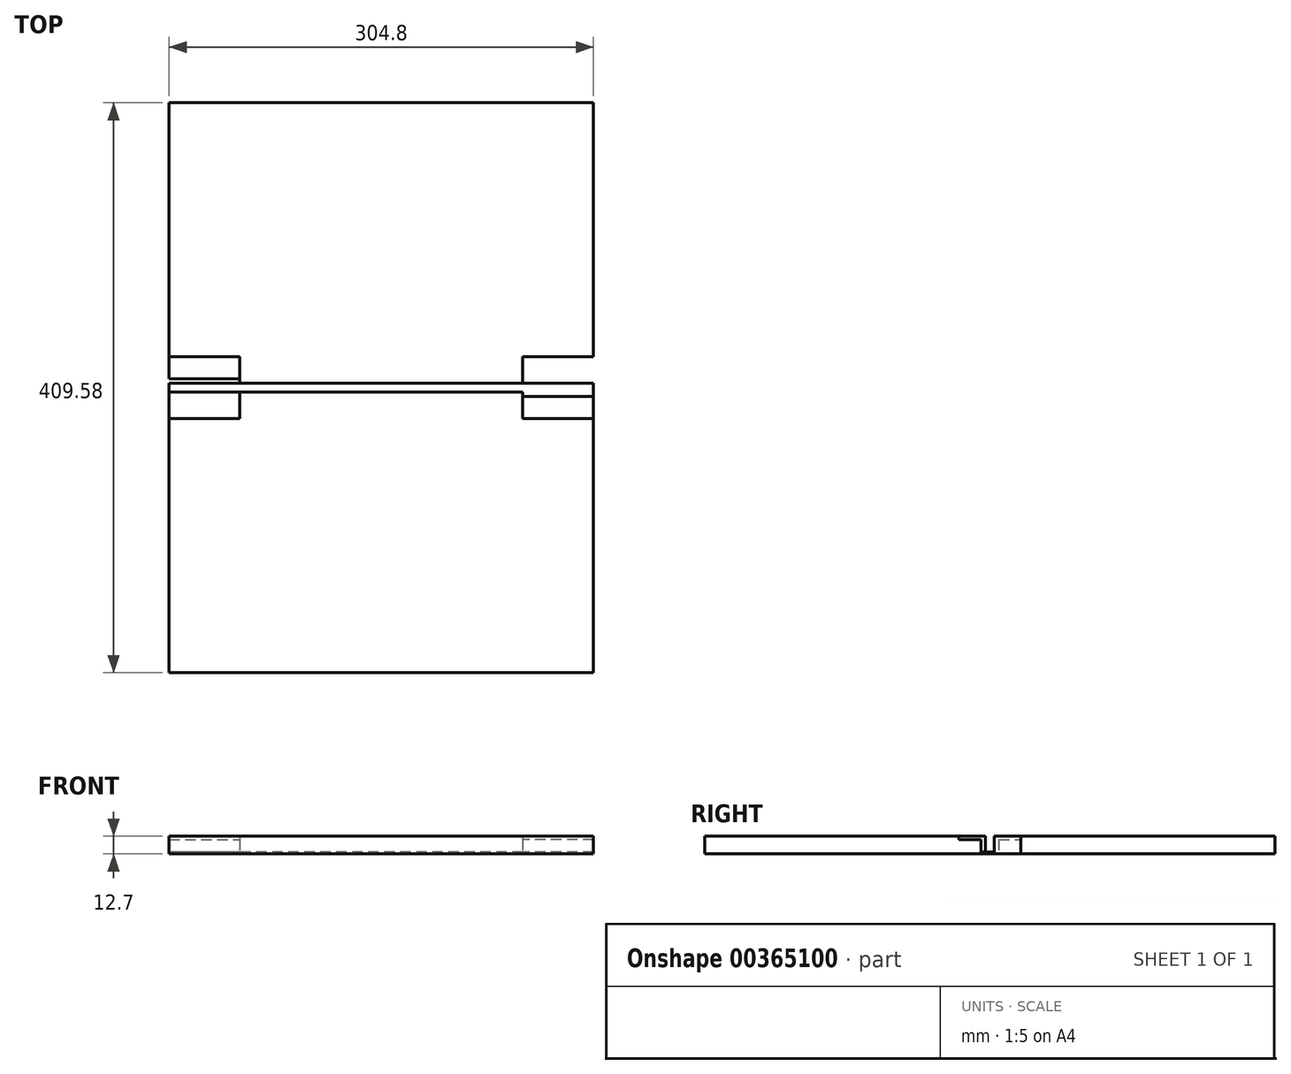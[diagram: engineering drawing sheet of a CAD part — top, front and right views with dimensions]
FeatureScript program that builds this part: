
annotation { "Feature Type Name" : "Feature", "Feature Type Description" : "" }
export const myFeature = defineFeature(function(context is Context, id is Id, definition is map)
    precondition{}
    {
        {
            var Q0;
            Q0=qCreatedBy(makeId("Top.planeOp"),FACE);
            var sketch = newSketch(context, id + "F0", { "sketchPlane" : qUnion([Q0])});
            skLineSegment(sketch, "E0.bottom", {"start": v(152.4, -204.79) * mm, "end": v(-152.4, -204.79) * mm});
            skLineSegment(sketch, "E0.top", {"start": v(152.4, 204.79) * mm, "end": v(-152.4, 204.79) * mm});
            skLineSegment(sketch, "E0.left", {"start": v(152.4, -204.79) * mm, "end": v(152.4, 204.79) * mm});
            skLineSegment(sketch, "E0.right", {"start": v(-152.4, -204.79) * mm, "end": v(-152.4, 204.79) * mm});
            skPoint(sketch, "E0.middle", {"position": v(0, 0) * mm});
            skLineSegment(sketch, "E1.bottom", {"start": v(152.4, -3.18) * mm, "end": v(-152.4, -3.18) * mm});
            skLineSegment(sketch, "E1.top", {"start": v(152.4, 3.18) * mm, "end": v(-152.4, 3.18) * mm});
            skLineSegment(sketch, "E1.left", {"start": v(152.4, -3.18) * mm, "end": v(152.4, 3.18) * mm});
            skLineSegment(sketch, "E1.right", {"start": v(-152.4, -3.18) * mm, "end": v(-152.4, 3.18) * mm});
            skPoint(sketch, "E2", {"position": v(-152.4, 0) * mm});
            skLineSegment(sketch, "E3", {"start": v(-152.4, 0) * mm, "end": v(0, 0) * mm});
            skLineSegment(sketch, "E4.bottom", {"start": v(-152.4, 3.18) * mm, "end": v(-101.6, 3.18) * mm});
            skLineSegment(sketch, "E4.top", {"start": v(-152.4, 22.23) * mm, "end": v(-101.6, 22.23) * mm});
            skLineSegment(sketch, "E4.left", {"start": v(-152.4, 3.18) * mm, "end": v(-152.4, 22.23) * mm});
            skLineSegment(sketch, "E4.right", {"start": v(-101.6, 3.18) * mm, "end": v(-101.6, 22.22) * mm});
            skLineSegment(sketch, "E5.top", {"start": v(-152.4, 6.35) * mm, "end": v(-101.6, 6.35) * mm});
            skLineSegment(sketch, "E5.left", {"start": v(-152.4, 3.18) * mm, "end": v(-152.4, 6.35) * mm});
            skLineSegment(sketch, "E5.right", {"start": v(-101.6, 3.18) * mm, "end": v(-101.6, 6.35) * mm});
            skLineSegment(sketch, "E6.MirrorCS", {"start": v(-152.4, 3.18) * mm, "end": v(-152.4, -3.18) * mm});
            skLineSegment(sketch, "E7.MirrorCS", {"start": v(-101.6, -3.18) * mm, "end": v(-101.6, -22.22) * mm});
            skLineSegment(sketch, "E8.MirrorCS", {"start": v(-101.6, -3.18) * mm, "end": v(-101.6, -6.35) * mm});
            skLineSegment(sketch, "E9.MirrorCS", {"start": v(-152.4, -3.18) * mm, "end": v(-152.4, -22.23) * mm});
            skLineSegment(sketch, "E10.MirrorCS", {"start": v(-152.4, -3.18) * mm, "end": v(-152.4, -6.35) * mm});
            skLineSegment(sketch, "E11.MirrorCS", {"start": v(-152.4, -6.35) * mm, "end": v(-101.6, -6.35) * mm});
            skLineSegment(sketch, "E12.MirrorCS", {"start": v(-152.4, -22.23) * mm, "end": v(-101.6, -22.22) * mm});
            skLineSegment(sketch, "E13.MirrorCS", {"start": v(-152.4, -3.18) * mm, "end": v(-101.6, -3.17) * mm});
            skPoint(sketch, "E14", {"position": v(0, 3.18) * mm});
            skPoint(sketch, "E15.MirrorP", {"position": v(152.4, 0) * mm});
            skLineSegment(sketch, "E16.MirrorCS", {"start": v(152.4, 3.18) * mm, "end": v(152.4, 22.23) * mm});
            skLineSegment(sketch, "E17.MirrorCS", {"start": v(152.4, 3.18) * mm, "end": v(152.4, -3.18) * mm});
            skLineSegment(sketch, "E18.MirrorCS", {"start": v(152.4, -6.35) * mm, "end": v(101.6, -6.35) * mm});
            skLineSegment(sketch, "E19.MirrorCS", {"start": v(152.4, -22.22) * mm, "end": v(101.6, -22.22) * mm});
            skLineSegment(sketch, "E20.MirrorCS", {"start": v(152.4, 3.18) * mm, "end": v(101.6, 3.17) * mm});
            skLineSegment(sketch, "E21.MirrorCS", {"start": v(101.6, 3.18) * mm, "end": v(101.6, 22.22) * mm});
            skLineSegment(sketch, "E22.MirrorCS", {"start": v(101.6, -3.18) * mm, "end": v(101.6, -6.35) * mm});
            skLineSegment(sketch, "E23.MirrorCS", {"start": v(152.4, -3.17) * mm, "end": v(101.6, -3.17) * mm});
            skLineSegment(sketch, "E24.MirrorCS", {"start": v(101.6, 3.18) * mm, "end": v(101.6, 6.35) * mm});
            skLineSegment(sketch, "E25.MirrorCS", {"start": v(152.4, -3.18) * mm, "end": v(152.4, -6.35) * mm});
            skLineSegment(sketch, "E26.MirrorCS", {"start": v(152.4, 6.35) * mm, "end": v(101.6, 6.35) * mm});
            skLineSegment(sketch, "E27.MirrorCS", {"start": v(101.6, -3.18) * mm, "end": v(101.6, -22.22) * mm});
            skLineSegment(sketch, "E28.MirrorCS", {"start": v(152.4, 22.23) * mm, "end": v(101.6, 22.22) * mm});
            skLineSegment(sketch, "E29.MirrorCS", {"start": v(152.4, 3.18) * mm, "end": v(152.4, 6.35) * mm});
            skLineSegment(sketch, "E30.MirrorCS", {"start": v(152.4, -3.18) * mm, "end": v(152.4, -22.23) * mm});
            skSolve(sketch);
        }
        {
            var Q0;
            Q0=makeQuery(id+"F0.imprint","IMPRINT",FACE,{"disambiguationData":[TD([[makeQuery(id+"F0.imprint","IMPRINT",EDGE,{"derivedFrom":sQuery(id+"F0.wireOp",EDGE,"E4.bottom")}),1.0]])]});
            var Q1;
            Q1=makeQuery(id+"F0.imprint","IMPRINT",FACE,{"disambiguationData":[TD([[makeQuery(id+"F0.imprint","IMPRINT",EDGE,{"derivedFrom":sQuery(id+"F0.wireOp",EDGE,"E1.bottom")}),-1.0]])]});
            var Q2;
            Q2=makeQuery(id+"F0.imprint","IMPRINT",FACE,{"disambiguationData":[TD([[makeQuery(id+"F0.imprint","IMPRINT",EDGE,{"derivedFrom":sQuery(id+"F0.wireOp",EDGE,"E8.MirrorCS")}),-1.0]])]});
            var Q3;
            {var subQ0=sQuery(id+"F0.wireOp",EDGE,"E18.MirrorCS");Q3=makeQuery(id+"F0.imprint","IMPRINT",FACE,{"disambiguationData":[TD([[makeQuery(id+"F0.imprint","IMPRINT",EDGE,{"derivedFrom":subQ0}),-1.0]])]});}
            var Q4;
            Q4=makeQuery(id+"F0.imprint","IMPRINT",FACE,{"disambiguationData":[TD([[makeQuery(id+"F0.imprint","IMPRINT",EDGE,{"derivedFrom":sQuery(id+"F0.wireOp",EDGE,"E20.MirrorCS")}),-1.0]])]});
            extrude(context, id + "F1", {"entities" : qUnion([Q0, Q1, Q2, Q3, Q4]), "depth" : 1.27 * mm});
        }
        {
            var Q0;
            {var subQ1=sQuery(id+"F0.wireOp",EDGE,"E0.top");Q0=makeQuery(id+"F0.imprint","IMPRINT",FACE,{"disambiguationData":[TD([[makeQuery(id+"F0.imprint","IMPRINT",EDGE,{"derivedFrom":subQ1}),1.0]])]});}
            var Q1;
            {var subQ2=sQuery(id+"F0.wireOp",EDGE,"E0.bottom");Q1=makeQuery(id+"F0.imprint","IMPRINT",FACE,{"disambiguationData":[TD([[makeQuery(id+"F0.imprint","IMPRINT",EDGE,{"derivedFrom":subQ2}),-1.0]])]});}
            extrude(context, id + "F2", {"entities" : qUnion([Q0, Q1]), "operationType" : NewBodyOperationType.ADD, "depth" : 12.7 * mm});
        }
        {
            var Q0;
            Q0=makeQuery(id+"F0.imprint","IMPRINT",FACE,{"disambiguationData":[TD([[makeQuery(id+"F0.imprint","IMPRINT",EDGE,{"derivedFrom":sQuery(id+"F0.wireOp",EDGE,"E4.top")}),-1.0]])]});
            var Q1;
            Q1=makeQuery(id+"F0.imprint","IMPRINT",FACE,{"disambiguationData":[TD([[makeQuery(id+"F0.imprint","IMPRINT",EDGE,{"derivedFrom":sQuery(id+"F0.wireOp",EDGE,"E7.MirrorCS")}),-1.0]])]});
            var Q2;
            {var subQ0=sQuery(id+"F0.wireOp",EDGE,"E18.MirrorCS");Q2=makeQuery(id+"F0.imprint","IMPRINT",FACE,{"disambiguationData":[TD([[makeQuery(id+"F0.imprint","IMPRINT",EDGE,{"derivedFrom":subQ0}),1.0]])]});}
            var Q3;
            Q3=makeQuery(id+"F0.imprint","IMPRINT",FACE,{"disambiguationData":[TD([[makeQuery(id+"F0.imprint","IMPRINT",EDGE,{"derivedFrom":sQuery(id+"F0.wireOp",EDGE,"E16.MirrorCS")}),1.0]])]});
            extrude(context, id + "F3", {"entities" : qUnion([Q0, Q1, Q2, Q3]), "operationType" : NewBodyOperationType.ADD, "depth" : 10.16 * mm});
        }
    });
